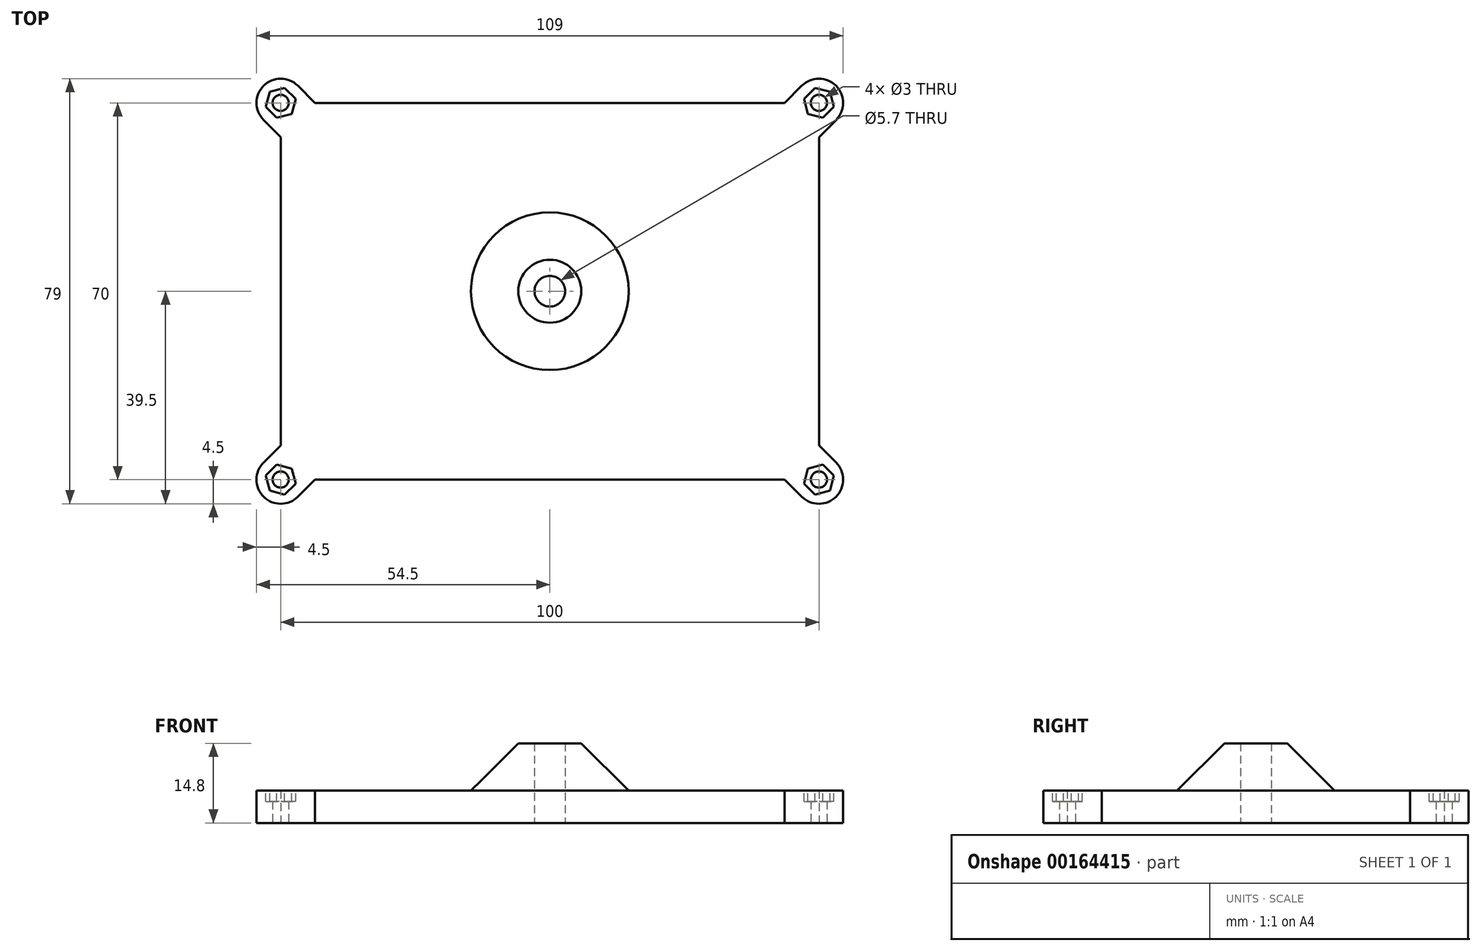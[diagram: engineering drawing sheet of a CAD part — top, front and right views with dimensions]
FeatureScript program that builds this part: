
annotation { "Feature Type Name" : "Feature", "Feature Type Description" : "" }
export const myFeature = defineFeature(function(context is Context, id is Id, definition is map)
    precondition{}
    {
        {
            var Q0;
            Q0=qCreatedBy(makeId("Top.planeOp"),FACE);
            var sketch = newSketch(context, id + "F0", { "sketchPlane" : qUnion([Q0])});
            skCircle(sketch, "E0", {"center": v(0, 0) * mm, "radius": 2.85 * mm});
            skLineSegment(sketch, "E1.bottom", {"start": v(50, -35) * mm, "end": v(-50, -35) * mm});
            skLineSegment(sketch, "E1.top", {"start": v(50, 35) * mm, "end": v(-50, 35) * mm});
            skLineSegment(sketch, "E1.left", {"start": v(50, -35) * mm, "end": v(50, 35) * mm});
            skLineSegment(sketch, "E1.right", {"start": v(-50, -35) * mm, "end": v(-50, 35) * mm});
            skLineSegment(sketch, "E2", {"start": v(43.64, 35) * mm, "end": v(46.82, 38.18) * mm});
            skLineSegment(sketch, "E3", {"start": v(50, 28.64) * mm, "end": v(53.18, 31.82) * mm});
            skArc(sketch, "E4", {"start": v(46.82, 38.18) * mm, "mid": v(53.18, 38.18) * mm, "end": v(53.18, 31.82) * mm});
            skCircle(sketch, "E5", {"center": v(50, 35) * mm, "radius": 1.5 * mm});
            skLineSegment(sketch, "E6", {"start": v(0, 46.33) * mm, "end": v(0, 0) * mm, "construction": true});
            skLineSegment(sketch, "E7", {"start": v(65.07, 0) * mm, "end": v(0, 0) * mm, "construction": true});
            skLineSegment(sketch, "E8.MirrorCS", {"start": v(-43.64, 35) * mm, "end": v(-46.82, 38.18) * mm});
            skArc(sketch, "E9.MirrorCS", {"start": v(-46.82, 38.18) * mm, "mid": v(-53.18, 38.18) * mm, "end": v(-53.18, 31.82) * mm});
            skCircle(sketch, "E10.MirrorC", {"center": v(-50, 35) * mm, "radius": 1.5 * mm});
            skLineSegment(sketch, "E11.MirrorCS", {"start": v(-50, 28.64) * mm, "end": v(-53.18, 31.82) * mm});
            skLineSegment(sketch, "E12.MirrorCS", {"start": v(50, -28.64) * mm, "end": v(53.18, -31.82) * mm});
            skArc(sketch, "E13.MirrorCS", {"start": v(46.82, -38.18) * mm, "mid": v(53.18, -38.18) * mm, "end": v(53.18, -31.82) * mm});
            skCircle(sketch, "E14.MirrorC", {"center": v(50, -35) * mm, "radius": 1.5 * mm});
            skLineSegment(sketch, "E15.MirrorCS", {"start": v(43.64, -35) * mm, "end": v(46.82, -38.18) * mm});
            skLineSegment(sketch, "E16.MirrorCS", {"start": v(-43.64, -35) * mm, "end": v(-46.82, -38.18) * mm});
            skArc(sketch, "E17.MirrorCS", {"start": v(-46.82, -38.18) * mm, "mid": v(-53.18, -38.18) * mm, "end": v(-53.18, -31.82) * mm});
            skCircle(sketch, "E18.MirrorC", {"center": v(-50, -35) * mm, "radius": 1.5 * mm});
            skLineSegment(sketch, "E19.MirrorCS", {"start": v(-50, -28.64) * mm, "end": v(-53.18, -31.82) * mm});
            skSolve(sketch);
        }
        {
            var Q0;
            {var subQ4=sQuery(id+"F0.wireOp",EDGE,"E8.MirrorCS");Q0=makeQuery(id+"F0.imprint","IMPRINT",FACE,{"disambiguationData":[TD([[makeQuery(id+"F0.imprint","IMPRINT",EDGE,{"derivedFrom":subQ4}),1.0]])]});}
            var Q1;
            Q1=makeQuery(id+"F0.imprint","IMPRINT",FACE,{"disambiguationData":[TD([[makeQuery(id+"F0.imprint","IMPRINT",EDGE,{"derivedFrom":sQuery(id+"F0.wireOp",EDGE,"E0")}),-1.0]])]});
            var Q2;
            {var subQ4=sQuery(id+"F0.wireOp",EDGE,"E16.MirrorCS");Q2=makeQuery(id+"F0.imprint","IMPRINT",FACE,{"disambiguationData":[TD([[makeQuery(id+"F0.imprint","IMPRINT",EDGE,{"derivedFrom":subQ4}),-1.0]])]});}
            var Q3;
            {var subQ0=sQuery(id+"F0.wireOp",EDGE,"E12.MirrorCS");Q3=makeQuery(id+"F0.imprint","IMPRINT",FACE,{"disambiguationData":[TD([[makeQuery(id+"F0.imprint","IMPRINT",EDGE,{"derivedFrom":subQ0}),-1.0]])]});}
            var Q4;
            {var subQ4=sQuery(id+"F0.wireOp",EDGE,"E2");Q4=makeQuery(id+"F0.imprint","IMPRINT",FACE,{"disambiguationData":[TD([[makeQuery(id+"F0.imprint","IMPRINT",EDGE,{"derivedFrom":subQ4}),-1.0]])]});}
            extrude(context, id + "F1", {"entities" : qUnion([Q0, Q1, Q2, Q3, Q4]), "depth" : 6 * mm});
        }
        {
            var Q0;
            Q0=makeQuery(id+"F1.opExtrude","CAP_FACE",FACE,{"disambiguationData":[OSD([sQuery(id+"F0.wireOp",EDGE,"E0"),sQuery(id+"F0.wireOp",EDGE,"E1.bottom"),sQuery(id+"F0.wireOp",EDGE,"E1.top"),sQuery(id+"F0.wireOp",EDGE,"E1.left"),sQuery(id+"F0.wireOp",EDGE,"E1.right"),sQuery(id+"F0.wireOp",EDGE,"E2"),sQuery(id+"F0.wireOp",EDGE,"E3"),sQuery(id+"F0.wireOp",EDGE,"E4"),sQuery(id+"F0.wireOp",EDGE,"E5"),sQuery(id+"F0.wireOp",EDGE,"E8.MirrorCS"),sQuery(id+"F0.wireOp",EDGE,"E9.MirrorCS"),sQuery(id+"F0.wireOp",EDGE,"E10.MirrorC"),sQuery(id+"F0.wireOp",EDGE,"E11.MirrorCS"),sQuery(id+"F0.wireOp",EDGE,"E12.MirrorCS"),sQuery(id+"F0.wireOp",EDGE,"E13.MirrorCS"),sQuery(id+"F0.wireOp",EDGE,"E14.MirrorC"),sQuery(id+"F0.wireOp",EDGE,"E15.MirrorCS"),sQuery(id+"F0.wireOp",EDGE,"E16.MirrorCS"),sQuery(id+"F0.wireOp",EDGE,"E17.MirrorCS"),sQuery(id+"F0.wireOp",EDGE,"E18.MirrorC"),sQuery(id+"F0.wireOp",EDGE,"E19.MirrorCS")])],"isStart":false});
            var sketch = newSketch(context, id + "F2", { "sketchPlane" : qUnion([Q0])});
            skCircle(sketch, "E20.cCircle", {"center": v(-50, 35) * mm, "radius": 2.5 * mm, "construction": true});
            skLineSegment(sketch, "E20.0", {"start": v(-49.25, 37.79) * mm, "end": v(-47.21, 35.75) * mm});
            skLineSegment(sketch, "E20.1", {"start": v(-47.21, 35.75) * mm, "end": v(-47.96, 32.96) * mm});
            skLineSegment(sketch, "E20.2", {"start": v(-47.96, 32.96) * mm, "end": v(-50.75, 32.21) * mm});
            skLineSegment(sketch, "E20.3", {"start": v(-50.75, 32.21) * mm, "end": v(-52.79, 34.25) * mm});
            skLineSegment(sketch, "E20.4", {"start": v(-52.79, 34.25) * mm, "end": v(-52.04, 37.04) * mm});
            skLineSegment(sketch, "E20.5", {"start": v(-52.04, 37.04) * mm, "end": v(-49.25, 37.79) * mm});
            skPoint(sketch, "E20.0.midPoint", {"position": v(-48.23, 36.77) * mm});
            skLineSegment(sketch, "E21", {"start": v(0, 0) * mm, "end": v(0, 64.6) * mm, "construction": true});
            skLineSegment(sketch, "E22", {"start": v(0.93, 0) * mm, "end": v(75.83, 0) * mm, "construction": true});
            skLineSegment(sketch, "E23.MirrorCS", {"start": v(52.79, 34.25) * mm, "end": v(52.04, 37.04) * mm});
            skLineSegment(sketch, "E24.MirrorCS", {"start": v(50.75, 32.21) * mm, "end": v(52.79, 34.25) * mm});
            skLineSegment(sketch, "E25.MirrorCS", {"start": v(49.25, 37.79) * mm, "end": v(47.21, 35.75) * mm});
            skLineSegment(sketch, "E26.MirrorCS", {"start": v(52.04, 37.04) * mm, "end": v(49.25, 37.79) * mm});
            skLineSegment(sketch, "E27.MirrorCS", {"start": v(47.21, 35.75) * mm, "end": v(47.96, 32.96) * mm});
            skLineSegment(sketch, "E28.MirrorCS", {"start": v(47.96, 32.96) * mm, "end": v(50.75, 32.21) * mm});
            skCircle(sketch, "E29.MirrorC", {"center": v(50, 35) * mm, "radius": 2.5 * mm, "construction": true});
            skPoint(sketch, "E30.MirrorP", {"position": v(48.23, 36.77) * mm});
            skLineSegment(sketch, "E31.MirrorCS", {"start": v(-50.75, -32.21) * mm, "end": v(-52.79, -34.25) * mm});
            skLineSegment(sketch, "E32.MirrorCS", {"start": v(-49.25, -37.79) * mm, "end": v(-47.21, -35.75) * mm});
            skLineSegment(sketch, "E33.MirrorCS", {"start": v(50.75, -32.21) * mm, "end": v(52.79, -34.25) * mm});
            skLineSegment(sketch, "E34.MirrorCS", {"start": v(49.25, -37.79) * mm, "end": v(47.21, -35.75) * mm});
            skLineSegment(sketch, "E35.MirrorCS", {"start": v(-52.79, -34.25) * mm, "end": v(-52.04, -37.04) * mm});
            skLineSegment(sketch, "E36.MirrorCS", {"start": v(-47.96, -32.96) * mm, "end": v(-50.75, -32.21) * mm});
            skLineSegment(sketch, "E37.MirrorCS", {"start": v(-47.21, -35.75) * mm, "end": v(-47.96, -32.96) * mm});
            skLineSegment(sketch, "E38.MirrorCS", {"start": v(47.21, -35.75) * mm, "end": v(47.96, -32.96) * mm});
            skLineSegment(sketch, "E39.MirrorCS", {"start": v(52.04, -37.04) * mm, "end": v(49.25, -37.79) * mm});
            skLineSegment(sketch, "E40.MirrorCS", {"start": v(-52.04, -37.04) * mm, "end": v(-49.25, -37.79) * mm});
            skCircle(sketch, "E41.MirrorC", {"center": v(-50, -35) * mm, "radius": 2.5 * mm, "construction": true});
            skCircle(sketch, "E42.MirrorC", {"center": v(50, -35) * mm, "radius": 2.5 * mm, "construction": true});
            skLineSegment(sketch, "E43.MirrorCS", {"start": v(47.96, -32.96) * mm, "end": v(50.75, -32.21) * mm});
            skPoint(sketch, "E44.MirrorP", {"position": v(-48.23, -36.77) * mm});
            skPoint(sketch, "E45.MirrorP", {"position": v(48.23, -36.77) * mm});
            skLineSegment(sketch, "E46.MirrorCS", {"start": v(52.79, -34.25) * mm, "end": v(52.04, -37.04) * mm});
            skSolve(sketch);
        }
        {
            var Q0;
            Q0=makeQuery(id+"F2.imprint","IMPRINT",FACE,{"disambiguationData":[TD([[makeQuery(id+"F2.imprint","IMPRINT",EDGE,{"derivedFrom":sQuery(id+"F2.wireOp",EDGE,"E20.0")}),-1.0]])]});
            var Q1;
            Q1=makeQuery(id+"F2.imprint","IMPRINT",FACE,{"disambiguationData":[TD([[makeQuery(id+"F2.imprint","IMPRINT",EDGE,{"derivedFrom":sQuery(id+"F2.wireOp",EDGE,"E23.MirrorCS")}),1.0]])]});
            var Q2;
            Q2=makeQuery(id+"F2.imprint","IMPRINT",FACE,{"disambiguationData":[TD([[makeQuery(id+"F2.imprint","IMPRINT",EDGE,{"derivedFrom":sQuery(id+"F2.wireOp",EDGE,"E33.MirrorCS")}),-1.0]])]});
            var Q3;
            Q3=makeQuery(id+"F2.imprint","IMPRINT",FACE,{"disambiguationData":[TD([[makeQuery(id+"F2.imprint","IMPRINT",EDGE,{"derivedFrom":sQuery(id+"F2.wireOp",EDGE,"E31.MirrorCS")}),1.0]])]});
            extrude(context, id + "F3", {"entities" : qUnion([Q0, Q1, Q2, Q3]), "operationType" : NewBodyOperationType.REMOVE, "oppositeDirection" : true, "depth" : 2 * mm});
        }
        {
            var Q0;
            Q0=qCreatedBy(makeId("Front.planeOp"),FACE);
            var sketch = newSketch(context, id + "F4", { "sketchPlane" : qUnion([Q0])});
            skLineSegment(sketch, "E47.0", {"start": v(-2.85, 6) * mm, "end": v(2.85, 6) * mm});
            skLineSegment(sketch, "E48", {"start": v(-2.85, 6) * mm, "end": v(-2.85, 14.8) * mm});
            skLineSegment(sketch, "E49", {"start": v(-2.85, 14.8) * mm, "end": v(-5.85, 14.8) * mm});
            skLineSegment(sketch, "E50", {"start": v(-5.85, 14.8) * mm, "end": v(-14.65, 6) * mm});
            skLineSegment(sketch, "E51", {"start": v(-14.65, 6) * mm, "end": v(-2.85, 6) * mm});
            skLineSegment(sketch, "E52", {"start": v(0, 0) * mm, "end": v(0, 27.48) * mm, "construction": true});
            skSolve(sketch);
        }
        {
            var Q0;
            Q0=makeQuery(id+"F4.imprint","IMPRINT",FACE,{"disambiguationData":[TD([[makeQuery(id+"F4.imprint","IMPRINT",EDGE,{"derivedFrom":sQuery(id+"F4.wireOp",EDGE,"E48")}),1.0]])]});
            var Q1;
            Q1=sQuery(id+"F4.wireOp",EDGE,"E52");
            revolve(context, id + "F5", {"operationType" : NewBodyOperationType.ADD, "entities" : qUnion([Q0]), "axis" : qUnion([Q1]), "revolveType" : RevolveType.FULL});
        }
    });
